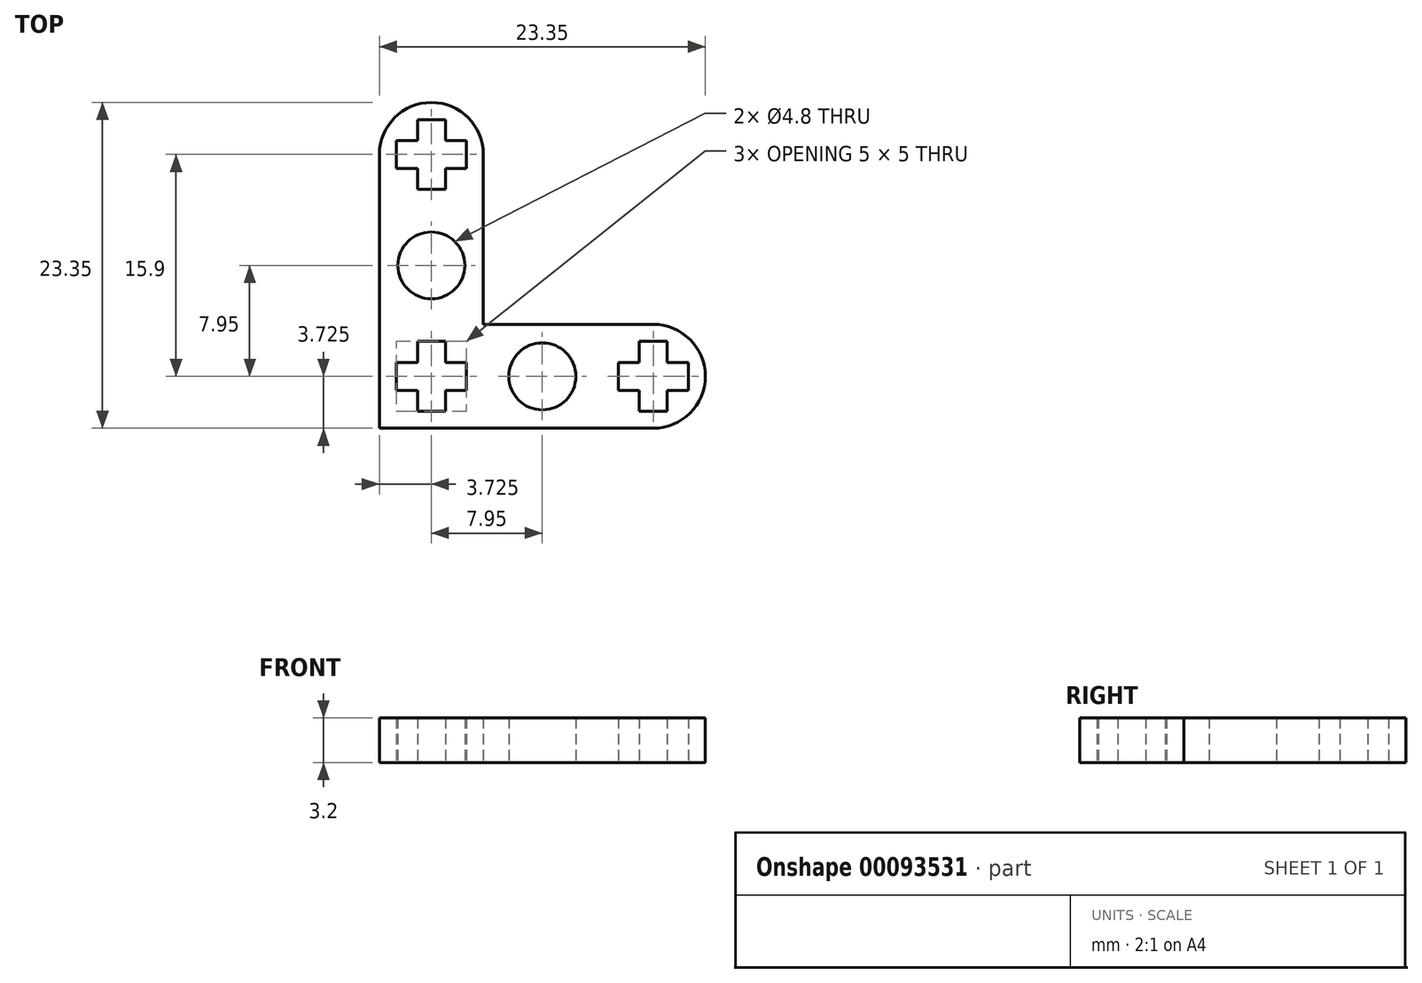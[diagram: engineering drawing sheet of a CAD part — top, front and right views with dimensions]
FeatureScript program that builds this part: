
annotation { "Feature Type Name" : "Feature", "Feature Type Description" : "" }
export const myFeature = defineFeature(function(context is Context, id is Id, definition is map)
    precondition{}
    {
        {
            var Q0;
            Q0=qCreatedBy(makeId("Top.planeOp"),FACE);
            var sketch = newSketch(context, id + "F0", { "sketchPlane" : qUnion([Q0])});
            skLineSegment(sketch, "E0.left", {"start": v(-7.45, 12.18) * mm, "end": v(-7.45, -7.45) * mm});
            skLineSegment(sketch, "E0.right", {"start": v(0, 12.18) * mm, "end": v(0, 0) * mm});
            skLineSegment(sketch, "E1.bottom", {"start": v(0, 0) * mm, "end": v(12.18, 0) * mm});
            skPoint(sketch, "E1.top.start.orphan", {"position": v(0, -7.45) * mm});
            skLineSegment(sketch, "E2", {"start": v(-7.45, -7.45) * mm, "end": v(12.18, -7.45) * mm});
            skLineSegment(sketch, "E3", {"start": v(-4.73, 14.68) * mm, "end": v(-2.73, 14.68) * mm});
            skLineSegment(sketch, "E4", {"start": v(-4.73, 9.68) * mm, "end": v(-2.73, 9.68) * mm});
            skLineSegment(sketch, "E5", {"start": v(-4.73, 14.68) * mm, "end": v(-4.73, 13.18) * mm});
            skLineSegment(sketch, "E6", {"start": v(-4.73, 13.18) * mm, "end": v(-6.23, 13.18) * mm});
            skLineSegment(sketch, "E7", {"start": v(-6.22, 13.18) * mm, "end": v(-6.22, 11.18) * mm});
            skLineSegment(sketch, "E8", {"start": v(-6.23, 11.18) * mm, "end": v(-4.73, 11.18) * mm});
            skLineSegment(sketch, "E9", {"start": v(-4.73, 11.18) * mm, "end": v(-4.73, 9.68) * mm});
            skLineSegment(sketch, "E10", {"start": v(-2.73, 9.68) * mm, "end": v(-2.73, 11.18) * mm});
            skLineSegment(sketch, "E11", {"start": v(-2.73, 11.18) * mm, "end": v(-1.23, 11.18) * mm});
            skLineSegment(sketch, "E12", {"start": v(-1.22, 11.18) * mm, "end": v(-1.22, 13.18) * mm});
            skLineSegment(sketch, "E13", {"start": v(-1.23, 13.18) * mm, "end": v(-2.73, 13.18) * mm});
            skLineSegment(sketch, "E14", {"start": v(-2.73, 13.18) * mm, "end": v(-2.73, 14.68) * mm});
            skLineSegment(sketch, "E15", {"start": v(-4.72, -1.22) * mm, "end": v(-2.73, -1.22) * mm});
            skLineSegment(sketch, "E16", {"start": v(-4.72, -6.22) * mm, "end": v(-2.73, -6.22) * mm});
            skLineSegment(sketch, "E17", {"start": v(-4.72, -1.22) * mm, "end": v(-4.72, -2.72) * mm});
            skLineSegment(sketch, "E18", {"start": v(-4.72, -2.72) * mm, "end": v(-6.22, -2.72) * mm});
            skLineSegment(sketch, "E19", {"start": v(-6.23, -2.72) * mm, "end": v(-6.23, -4.72) * mm});
            skLineSegment(sketch, "E20", {"start": v(-6.22, -4.72) * mm, "end": v(-4.72, -4.72) * mm});
            skLineSegment(sketch, "E21", {"start": v(-4.73, -4.72) * mm, "end": v(-4.72, -6.22) * mm});
            skLineSegment(sketch, "E22", {"start": v(-2.73, -6.22) * mm, "end": v(-2.73, -4.72) * mm});
            skLineSegment(sketch, "E23", {"start": v(-2.73, -4.72) * mm, "end": v(-1.23, -4.72) * mm});
            skLineSegment(sketch, "E24", {"start": v(-1.23, -4.72) * mm, "end": v(-1.23, -2.72) * mm});
            skLineSegment(sketch, "E25", {"start": v(-1.23, -2.72) * mm, "end": v(-2.72, -2.72) * mm});
            skLineSegment(sketch, "E26", {"start": v(-2.72, -2.72) * mm, "end": v(-2.73, -1.22) * mm});
            skPoint(sketch, "E27.top.start.orphan", {"position": v(2.52, -9.4) * mm});
            skLineSegment(sketch, "E28", {"start": v(11.18, -1.22) * mm, "end": v(13.18, -1.22) * mm});
            skLineSegment(sketch, "E29", {"start": v(11.18, -6.23) * mm, "end": v(13.18, -6.23) * mm});
            skLineSegment(sketch, "E30", {"start": v(11.18, -1.22) * mm, "end": v(11.18, -2.73) * mm});
            skLineSegment(sketch, "E31", {"start": v(11.18, -2.73) * mm, "end": v(9.68, -2.73) * mm});
            skLineSegment(sketch, "E32", {"start": v(9.68, -2.73) * mm, "end": v(9.68, -4.73) * mm});
            skLineSegment(sketch, "E33", {"start": v(9.68, -4.73) * mm, "end": v(11.18, -4.73) * mm});
            skLineSegment(sketch, "E34", {"start": v(11.18, -4.73) * mm, "end": v(11.18, -6.23) * mm});
            skLineSegment(sketch, "E35", {"start": v(13.18, -6.22) * mm, "end": v(13.18, -4.72) * mm});
            skLineSegment(sketch, "E36", {"start": v(13.18, -4.73) * mm, "end": v(14.68, -4.73) * mm});
            skLineSegment(sketch, "E37", {"start": v(14.68, -4.73) * mm, "end": v(14.68, -2.73) * mm});
            skLineSegment(sketch, "E38", {"start": v(14.68, -2.73) * mm, "end": v(13.18, -2.73) * mm});
            skLineSegment(sketch, "E39", {"start": v(13.18, -2.73) * mm, "end": v(13.18, -1.22) * mm});
            skArc(sketch, "E40", {"start": v(12.18, -7.45) * mm, "mid": v(15.9, -3.73) * mm, "end": v(12.18, 0) * mm});
            skLineSegment(sketch, "E41", {"start": v(12.18, 0) * mm, "end": v(12.18, -7.45) * mm, "construction": true});
            skPoint(sketch, "E42.orphan", {"position": v(16.09, -7.45) * mm});
            skArc(sketch, "E43", {"start": v(0, 12.18) * mm, "mid": v(-3.72, 15.9) * mm, "end": v(-7.45, 12.18) * mm});
            skLineSegment(sketch, "E44", {"start": v(-7.45, 12.18) * mm, "end": v(0, 12.18) * mm, "construction": true});
            skCircle(sketch, "E45", {"center": v(-3.72, 4.23) * mm, "radius": 2.4 * mm});
            skCircle(sketch, "E46", {"center": v(4.23, -3.73) * mm, "radius": 2.4 * mm});
            skSolve(sketch);
        }
        {
            var Q0;
            Q0 = qSketchRegion(id + "F0", true);
            extrude(context, id + "F1", {"entities" : qUnion([Q0]), "depth" : 3.2 * mm});
        }
    });
